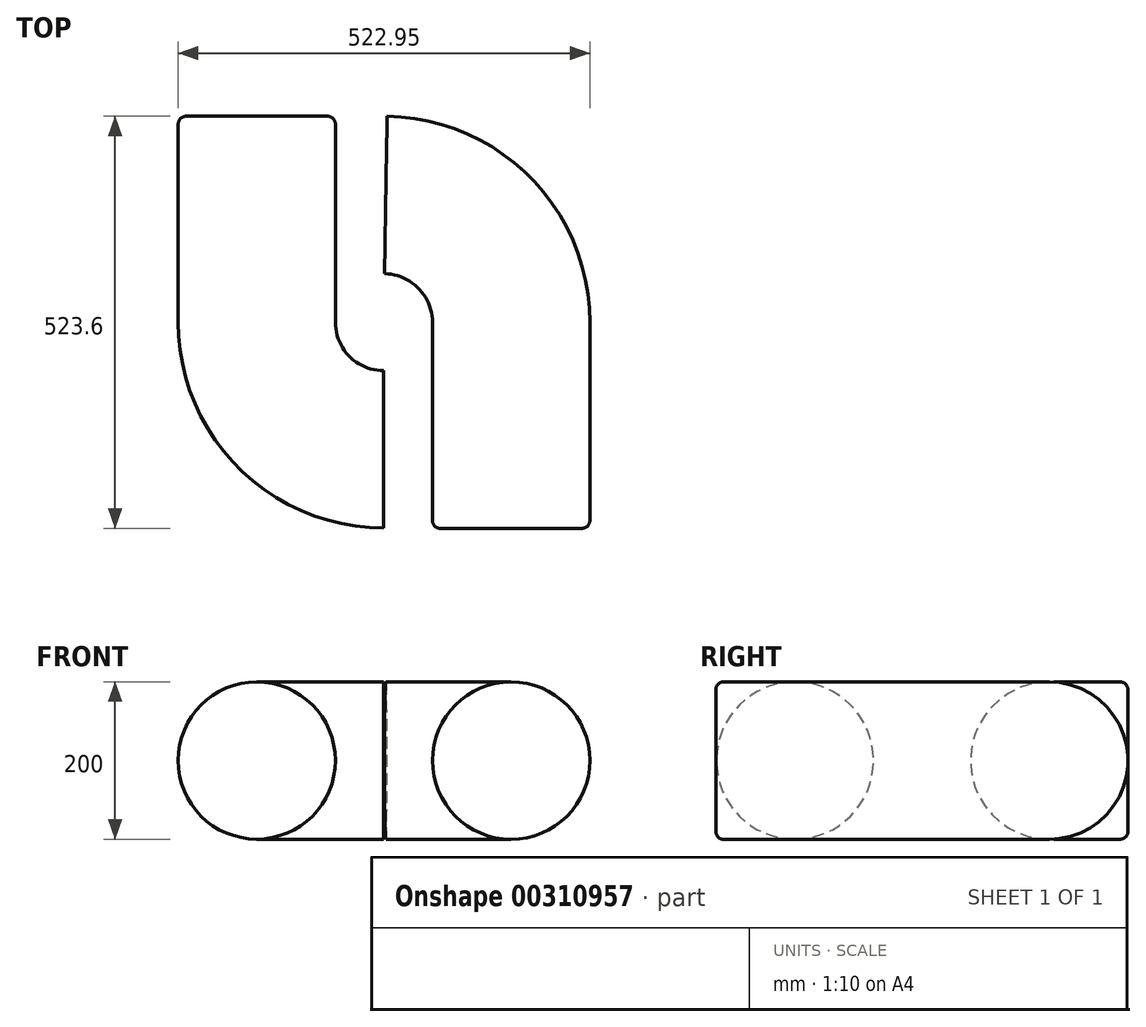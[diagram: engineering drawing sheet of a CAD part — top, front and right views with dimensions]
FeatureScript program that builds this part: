
annotation { "Feature Type Name" : "Feature", "Feature Type Description" : "" }
export const myFeature = defineFeature(function(context is Context, id is Id, definition is map)
    precondition{}
    {
        {
            var Q0;
            Q0=qCreatedBy(makeId("Top.planeOp"),FACE);
            var sketch = newSketch(context, id + "F0", { "sketchPlane" : qUnion([Q0])});
            skArc(sketch, "E0", {"start": v(161.8, 0) * mm, "mid": v(115.33, 113.48) * mm, "end": v(2.63, 161.78) * mm});
            skLineSegment(sketch, "E1", {"start": v(161.8, 0) * mm, "end": v(161.8, -261.8) * mm});
            skArc(sketch, "E2", {"start": v(0, -161.13) * mm, "mid": v(-113.94, -113.94) * mm, "end": v(-161.13, 0) * mm});
            skLineSegment(sketch, "E3", {"start": v(-161.13, 0) * mm, "end": v(-161.13, 261.8) * mm});
            skSolve(sketch);
        }
        {
            var Q0;
            Q0=qCreatedBy(makeId("Front.planeOp"),FACE);
            var sketch = newSketch(context, id + "F1", { "sketchPlane" : qUnion([Q0])});
            skCircle(sketch, "E4", {"center": v(161.8, 0) * mm, "radius": 100 * mm});
            skSolve(sketch);
        }
        {
            var Q0;
            Q0=makeQuery(id+"F1.imprint","IMPRINT",FACE,{"disambiguationData":[TD([[makeQuery(id+"F1.imprint","IMPRINT",EDGE,{"derivedFrom":sQuery(id+"F1.wireOp",EDGE,"E4")}),1.0]])]});
            var Q1;
            Q1=sQuery(id+"F0.wireOp",EDGE,"E0");
            sweep(context, id + "F2", {"profiles" : qUnion([Q0]), "path" : qUnion([Q1])});
        }
        {
            var Q0;
            Q0=makeQuery(id+"F2.opSweep","CAP_FACE",FACE,{"disambiguationData":[OSD([sQuery(id+"F0.wireOp",VERTEX,"E0.start"),sQuery(id+"F1.wireOp",EDGE,"E4")])],"isStart":true});
            var Q1;
            Q1=sQuery(id+"F0.wireOp",EDGE,"E1");
            sweep(context, id + "F3", {"operationType" : NewBodyOperationType.ADD, "profiles" : qUnion([Q0]), "path" : qUnion([Q1])});
        }
        {
            var Q0;
            Q0=makeQuery(id+"F3.opSweep","CAP_FACE",FACE,{"disambiguationData":[OSD([sQuery(id+"F0.wireOp",VERTEX,"E0.start"),sQuery(id+"F0.wireOp",VERTEX,"E1.end"),sQuery(id+"F1.wireOp",EDGE,"E4")])],"isStart":false});
            var sketch = newSketch(context, id + "F4", { "sketchPlane" : qUnion([Q0])});
            skCircle(sketch, "E5", {"center": v(161.8, 0) * mm, "radius": 158.54 * mm});
            skCircle(sketch, "E6", {"center": v(161.8, 0) * mm, "radius": 100 * mm});
            skSolve(sketch);
        }
        {
            var Q0;
            Q0=makeQuery(id+"F4.imprint","IMPRINT",FACE,{"disambiguationData":[TD([[makeQuery(id+"F4.imprint","IMPRINT",EDGE,{"derivedFrom":sQuery(id+"F4.wireOp",EDGE,"E5")}),1.0]])]});
            extrude(context, id + "F5", {"entities" : qUnion([Q0]), "operationType" : NewBodyOperationType.REMOVE, "depth" : -261 * mm});
        }
        {
            var Q0;
            Q0=makeQuery(id+"F3.opSweep","CAP_EDGE",EDGE,{"disambiguationData":[OSD([sQuery(id+"F0.wireOp",VERTEX,"E0.start"),sQuery(id+"F0.wireOp",VERTEX,"E1.end"),sQuery(id+"F1.wireOp",EDGE,"E4")])],"isStart":false});
            var Q1;
            Q1=makeQuery(id+"F5.boolean.opBoolean","MERGE",FACE,{"derivedFrom":[makeQuery(id+"F3.opSweep","SWEPT_FACE",FACE,{"disambiguationData":[OSD([sQuery(id+"F0.wireOp",VERTEX,"E0.start"),sQuery(id+"F0.wireOp",EDGE,"E1"),sQuery(id+"F1.wireOp",EDGE,"E4")])]}),makeQuery(id+"F5.opExtrude","SWEPT_FACE",FACE,{"disambiguationData":[OSD([sQuery(id+"F4.wireOp",EDGE,"E6")])]})]});
            fillet(context, id + "F6", {"entities" : qUnion([Q0, Q1]), "radius" : 10 * mm, "tangentPropagation" : true, "allowEdgeOverflow" : false});
        }
        {
            var Q0;
            Q0=qCreatedBy(makeId("Right.planeOp"),FACE);
            var sketch = newSketch(context, id + "F7", { "sketchPlane" : qUnion([Q0])});
            skCircle(sketch, "E7", {"center": v(-161.3, 0) * mm, "radius": 99.84 * mm});
            skSolve(sketch);
        }
        {
            var Q0;
            Q0=makeQuery(id+"F7.imprint","IMPRINT",FACE,{"disambiguationData":[TD([[makeQuery(id+"F7.imprint","IMPRINT",EDGE,{"derivedFrom":sQuery(id+"F7.wireOp",EDGE,"E7")}),1.0]])]});
            var Q1;
            Q1=sQuery(id+"F0.wireOp",EDGE,"E2");
            var Q2;
            Q2=sQuery(id+"F0.wireOp",EDGE,"E3");
            sweep(context, id + "F8", {"profiles" : qUnion([Q0]), "path" : qUnion([Q1, Q2])});
        }
        {
            var Q0;
            Q0=makeQuery(id+"F8.opSweep","CAP_EDGE",EDGE,{"disambiguationData":[OSD([sQuery(id+"F0.wireOp",VERTEX,"E3.end"),sQuery(id+"F7.wireOp",EDGE,"E7")])],"isStart":false});
            fillet(context, id + "F9", {"entities" : qUnion([Q0]), "radius" : 10 * mm, "tangentPropagation" : true, "allowEdgeOverflow" : false});
        }
    });
